# Revit family: Desk_Screens-Teknion-CQCDD_Routes_Smooth_Felt_Double_Desk_Screen-R2019
name_source: partatom
category: Furniture
units: mm (PartAtom-declared; Revit-internal decimal feet)

## family parameters
Always vertical = Yes
Cut with Voids When Loaded = No
OmniClass Number = 23.40.20.00
OmniClass Title = General Furniture and Specialties
Room Calculation Point = No
Shared = Yes
Work Plane-Based = No

## types (4) — shared parameters
Assembly Code = E2020200
Manufacturer = Teknion
Manufacturer Fax = 416.661.4586
Part Number = CQCDD
Product Documentation Link = https://assets.teknion.com
Product Line = Routes
Product Page URL = https://www.teknion.com
Series = Routes
Sustainability Data = https://www.teknion.com
URL = www.teknion.com
Unit Weight URL = http://www.teknion.com
Warranty = http://www.teknion.com

## per-type parameters (varying)
| type | Actual Width | Datum Height | Description | Hardaware Offset | Height | Model | Width |
| 47" Datum Height, 60" Width | 59.5 " | 47 " | Smooth Felt Double Desk Screen, 47" Datum Height, 60" Width | 12 " | 47 " | CQCDD4760 | 60 " |
| 42" Datum Height, 60" Width | 59.5 " | 42 " | Smooth Felt Double Desk Screen, 42" Datum Height, 60" Width | 12 " | 42 " | CQCDD4260 | 60 " |
| 47" Datum Height, 48" Width | 47.5 " | 47 " | Smooth Felt Double Desk Screen, 47" Datum Height, 48" Width | 9.6 " | 47 " | CQCDD4748 | 48 " |
| 42" Datum Height, 48" Width | 47.5 " | 42 " | Smooth Felt Double Desk Screen, 42" Datum Height, 48" Width | 9.6 " | 42 " | CQCDD4248 | 48 " |

## geometry (parser evidence)
native form markers: Sweep x3
no freeform markers — native parametric forms only
